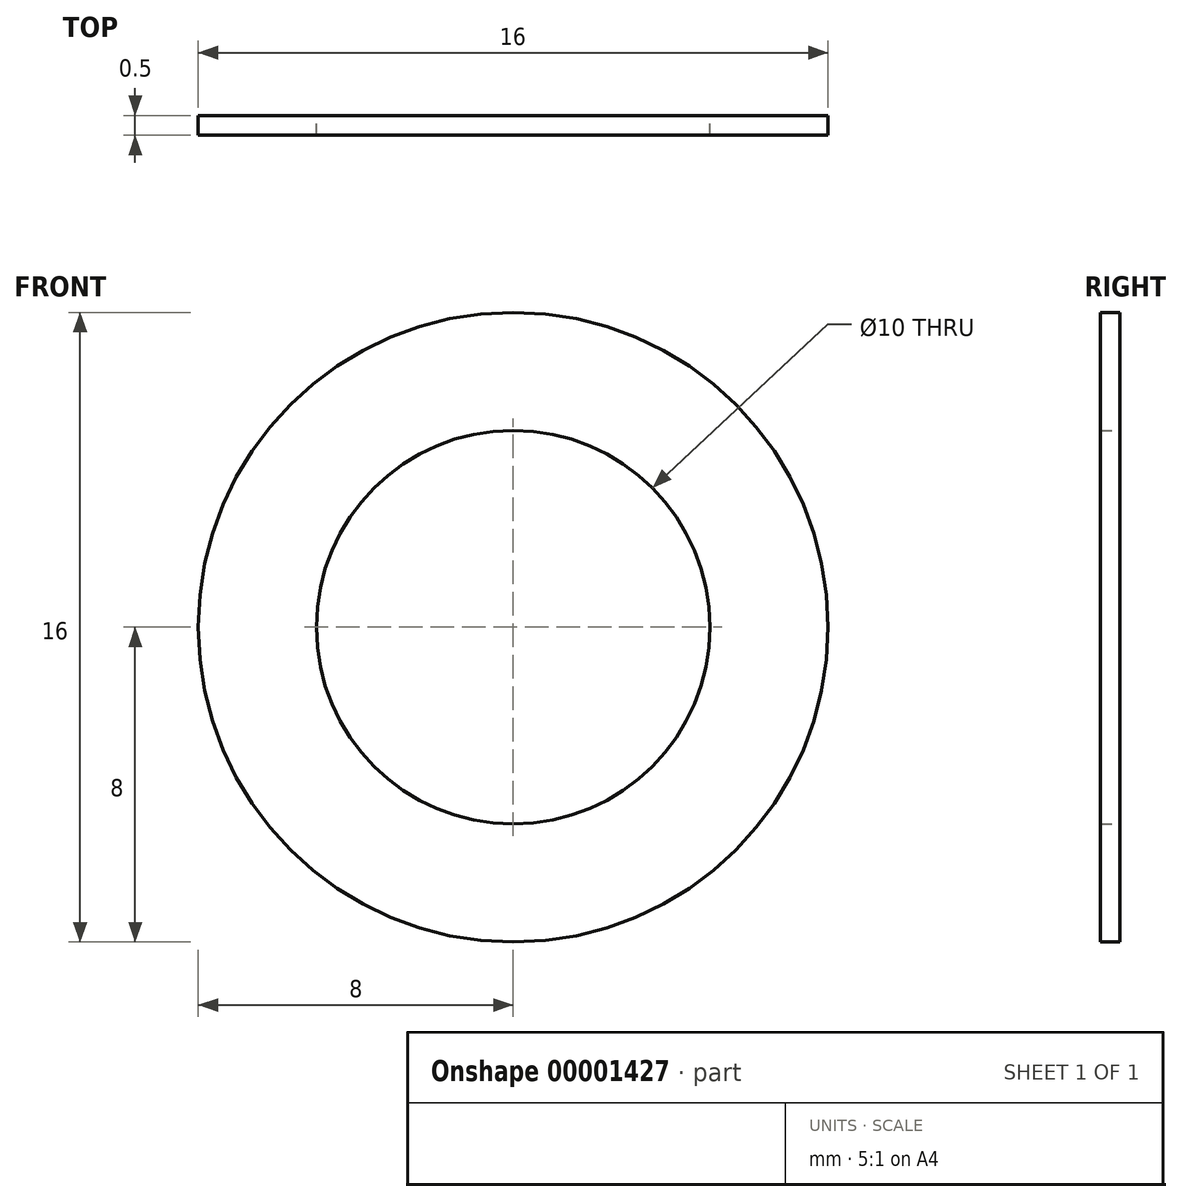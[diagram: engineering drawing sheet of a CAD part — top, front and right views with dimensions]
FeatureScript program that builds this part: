
annotation { "Feature Type Name" : "Feature", "Feature Type Description" : "" }
export const myFeature = defineFeature(function(context is Context, id is Id, definition is map)
    precondition{}
    {
        {
            var Q0;
            Q0=qCreatedBy(makeId("Front.planeOp"),FACE);
            var sketch = newSketch(context, id + "F0", { "sketchPlane" : qUnion([Q0])});
            skCircle(sketch, "E0", {"center": v(0, 0) * mm, "radius": 8 * mm});
            skCircle(sketch, "E1", {"center": v(0, 0) * mm, "radius": 5 * mm});
            skSolve(sketch);
        }
        {
            var Q0;
            Q0=makeQuery(id+"F0.imprint","IMPRINT",FACE,{"disambiguationData":[TD([[makeQuery(id+"F0.imprint","IMPRINT",EDGE,{"derivedFrom":sQuery(id+"F0.wireOp",EDGE,"E0")}),1.0]])]});
            extrude(context, id + "F1", {"entities" : qUnion([Q0]), "depth" : .5 * mm, "symmetric" : true});
        }
    });
